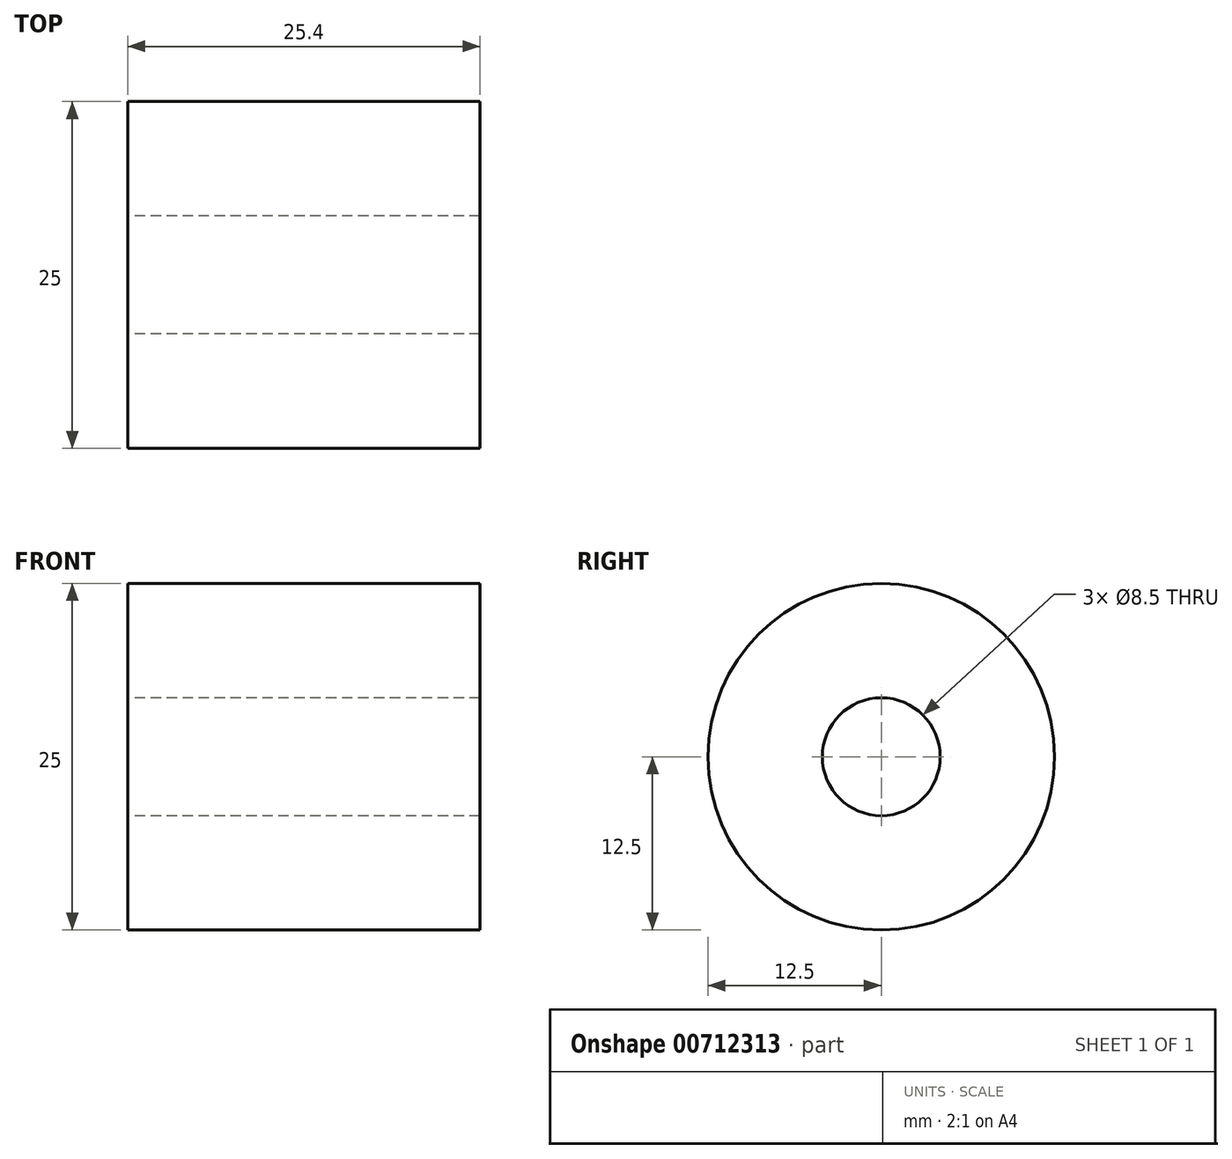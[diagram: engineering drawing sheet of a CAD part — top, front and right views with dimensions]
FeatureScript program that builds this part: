
annotation { "Feature Type Name" : "Feature", "Feature Type Description" : "" }
export const myFeature = defineFeature(function(context is Context, id is Id, definition is map)
    precondition{}
    {
        {
            var Q0;
            Q0=qCreatedBy(makeId("Right.planeOp"),FACE);
            var sketch = newSketch(context, id + "F0", { "sketchPlane" : qUnion([Q0])});
            skCircle(sketch, "E0", {"center": v(0, 0) * mm, "radius": 12.5 * mm});
            skCircle(sketch, "E1", {"center": v(0, 0) * mm, "radius": 4.25 * mm});
            skSolve(sketch);
        }
        {
            var Q0;
            Q0 = qSketchRegion(id + "F0", true);
            extrude(context, id + "F1", {"entities" : qUnion([Q0]), "depth" : 25.4 * mm, "offsetDistance" : 25 * mm});
        }
    });
